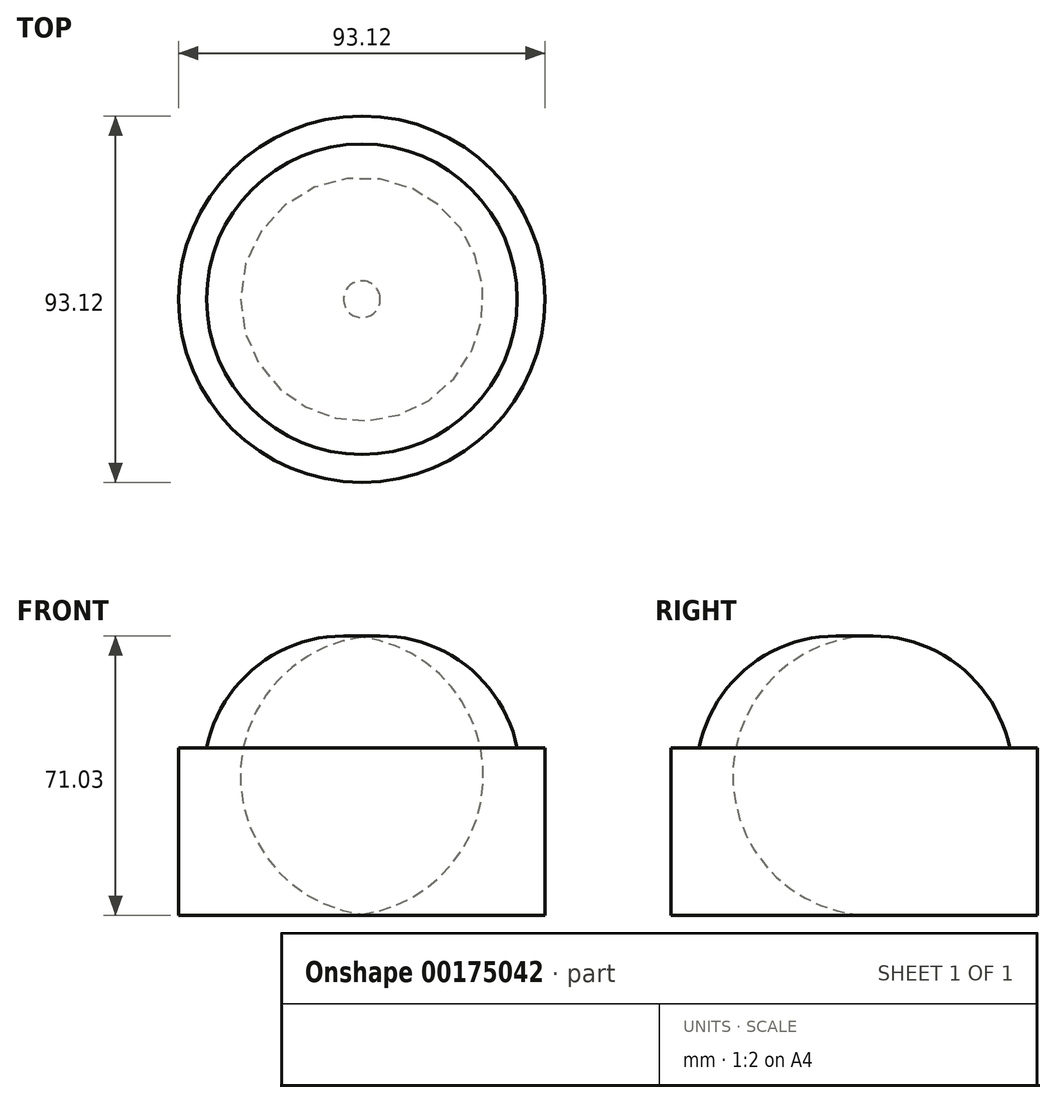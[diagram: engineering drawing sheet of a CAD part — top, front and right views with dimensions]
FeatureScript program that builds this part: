
annotation { "Feature Type Name" : "Feature", "Feature Type Description" : "" }
export const myFeature = defineFeature(function(context is Context, id is Id, definition is map)
    precondition{}
    {
        {
            var Q0;
            Q0=qCreatedBy(makeId("Front.planeOp"),FACE);
            var sketch = newSketch(context, id + "F0", { "sketchPlane" : qUnion([Q0])});
            skLineSegment(sketch, "E0", {"start": v(-46.56, 22.18) * mm, "end": v(-46.56, -20.46) * mm});
            skLineSegment(sketch, "E1", {"start": v(0, 42.52) * mm, "end": v(0, -49.87) * mm});
            skLineSegment(sketch, "E2", {"start": v(-46.56, 22.18) * mm, "end": v(-39.45, 22.18) * mm});
            skLineSegment(sketch, "E3", {"start": v(-46.56, -20.46) * mm, "end": v(-4.66, -20.46) * mm});
            skArc(sketch, "E4", {"start": v(-39.45, 22.18) * mm, "mid": v(-32.18, -7.4) * mm, "end": v(-4.66, -20.46) * mm});
            skSolve(sketch);
        }
        {
            var Q0;
            Q0 = qSketchRegion(id + "F0", true);
            var Q1;
            Q1=sQuery(id+"F0.wireOp",EDGE,"E1");
            revolve(context, id + "F1", {"entities" : qUnion([Q0]), "axis" : qUnion([Q1]), "revolveType" : RevolveType.FULL});
        }
        {
            var Q0;
            Q0=makeQuery(id+"F1.opRevolve","SWEPT_FACE",FACE,{"disambiguationData":[OSD([sQuery(id+"F0.wireOp",EDGE,"E3")])]});
            var sketch = newSketch(context, id + "F2", { "sketchPlane" : qUnion([Q0])});
            skCircle(sketch, "E5", {"center": v(0, 0) * mm, "radius": 4.66 * mm});
            skSolve(sketch);
        }
        {
            var Q0;
            Q0 = qSketchRegion(id + "F2", true);
            extrude(context, id + "F3", {"entities" : qUnion([Q0]), "operationType" : NewBodyOperationType.ADD, "oppositeDirection" : true, "depth" : 0.13 * mm});
        }
    });
